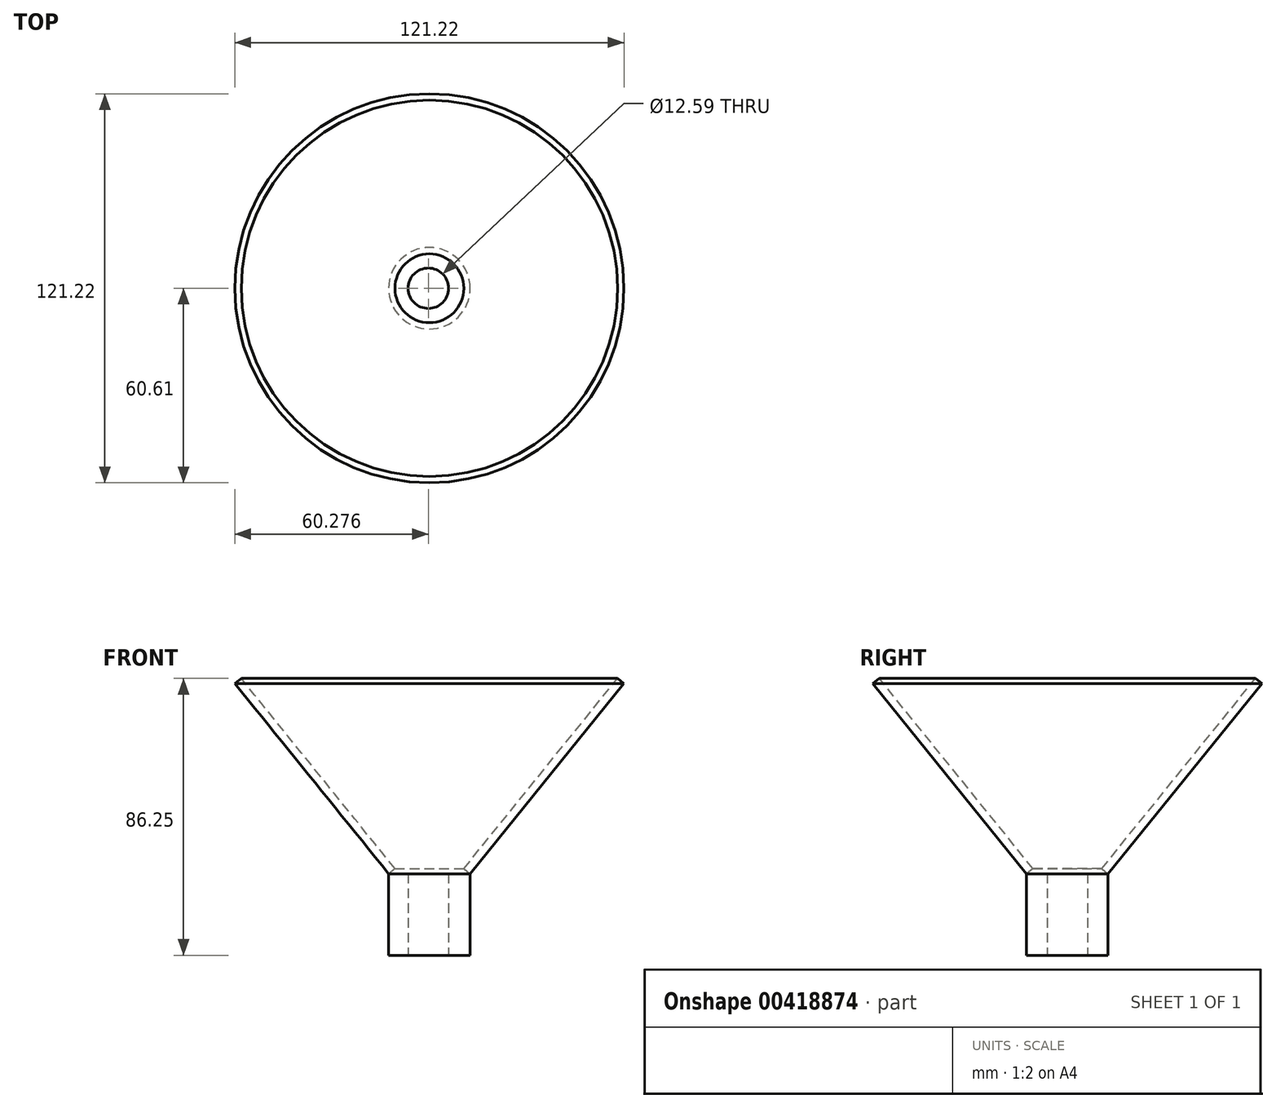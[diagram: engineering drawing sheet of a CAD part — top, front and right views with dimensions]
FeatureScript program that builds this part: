
annotation { "Feature Type Name" : "Feature", "Feature Type Description" : "" }
export const myFeature = defineFeature(function(context is Context, id is Id, definition is map)
    precondition{}
    {
        {
            var Q0;
            Q0=qCreatedBy(makeId("Front.planeOp"),FACE);
            var sketch = newSketch(context, id + "F0", { "sketchPlane" : qUnion([Q0])});
            skLineSegment(sketch, "E0", {"start": v(0, 0) * mm, "end": v(-12.7, 0) * mm});
            skLineSegment(sketch, "E1", {"start": v(0, 0) * mm, "end": v(0, 25.4) * mm});
            skLineSegment(sketch, "E2", {"start": v(-12.7, 0) * mm, "end": v(-12.7, 25.4) * mm});
            skLineSegment(sketch, "E3", {"start": v(0, 25.4) * mm, "end": v(-12.7, 25.4) * mm});
            skLineSegment(sketch, "E4", {"start": v(0, 25.4) * mm, "end": v(47.9, 84.66) * mm});
            skLineSegment(sketch, "E5", {"start": v(0, 25.4) * mm, "end": v(-1.98, 27) * mm});
            skLineSegment(sketch, "E6", {"start": v(-1.98, 27) * mm, "end": v(45.93, 86.25) * mm});
            skLineSegment(sketch, "E7", {"start": v(45.93, 86.25) * mm, "end": v(47.9, 84.66) * mm});
            skSolve(sketch);
        }
        {
            var Q0;
            Q0 = qSketchRegion(id + "F0", true);
            var Q1;
            Q1=sQuery(id+"F0.wireOp",EDGE,"E2");
            revolve(context, id + "F1", {"entities" : qUnion([Q0]), "axis" : qUnion([Q1]), "revolveType" : RevolveType.FULL});
        }
        {
            var Q0;
            Q0=makeQuery(id+"F1.opRevolve","SWEPT_FACE",FACE,{"disambiguationData":[OSD([sQuery(id+"F0.wireOp",EDGE,"E0")])]});
            var sketch = newSketch(context, id + "F2", { "sketchPlane" : qUnion([Q0])});
            skCircle(sketch, "E8", {"center": v(-12.7, 0) * mm, "radius": 12.7 * mm});
            skSolve(sketch);
        }
        {
            var Q0;
            Q0=makeQuery(id+"F2.imprint","IMPRINT",FACE,{"disambiguationData":[TD([[makeQuery(id+"F2.imprint","IMPRINT",EDGE,{"derivedFrom":sQuery(id+"F2.wireOp",EDGE,"E8")}),1.0]])]});
            var sketch = newSketch(context, id + "F3", { "sketchPlane" : qUnion([Q0])});
            skCircle(sketch, "E9", {"center": v(-13.03, 0) * mm, "radius": 6.3 * mm});
            skSolve(sketch);
        }
        {
            var Q0;
            Q0 = qSketchRegion(id + "F3", true);
            extrude(context, id + "F4", {"entities" : qUnion([Q0]), "operationType" : NewBodyOperationType.REMOVE, "oppositeDirection" : true, "depth" : 25.4 * mm});
        }
    });
